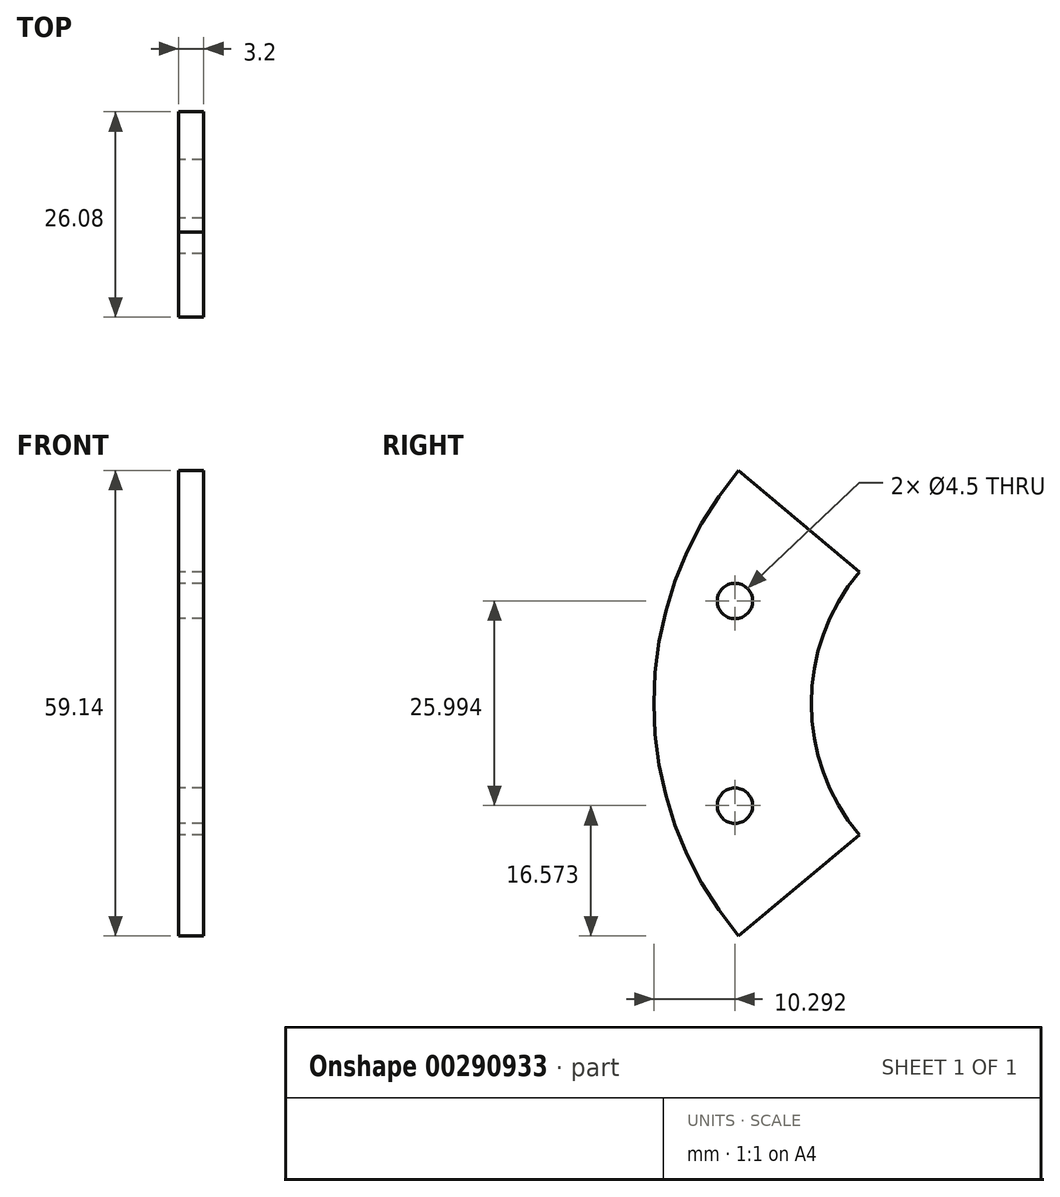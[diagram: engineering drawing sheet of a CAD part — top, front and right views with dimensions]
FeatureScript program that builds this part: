
annotation { "Feature Type Name" : "Feature", "Feature Type Description" : "" }
export const myFeature = defineFeature(function(context is Context, id is Id, definition is map)
    precondition{}
    {
        {
            var Q0;
            Q0=qCreatedBy(makeId("Right.planeOp"),FACE);
            var sketch = newSketch(context, id + "F0", { "sketchPlane" : qUnion([Q0])});
            skArc(sketch, "E0", {"start": v(-19.92, 16.71) * mm, "mid": v(-26, 0) * mm, "end": v(-19.92, -16.71) * mm});
            skArc(sketch, "E1", {"start": v(-35.24, 29.57) * mm, "mid": v(-46, 0) * mm, "end": v(-35.24, -29.57) * mm});
            skCircle(sketch, "E2", {"center": v(0, 0) * mm, "radius": 38 * mm, "construction": true});
            skLineSegment(sketch, "E3", {"start": v(-19.92, 16.71) * mm, "end": v(-35.24, 29.57) * mm});
            skLineSegment(sketch, "E4", {"start": v(0, 0) * mm, "end": v(-56.56, 20.59) * mm, "construction": true});
            skCircle(sketch, "E5", {"center": v(-35.7, 13) * mm, "radius": 2.25 * mm});
            skCircle(sketch, "E6.MirrorC", {"center": v(-35.7, -13) * mm, "radius": 2.25 * mm});
            skLineSegment(sketch, "E7.MirrorCS", {"start": v(-19.92, -16.71) * mm, "end": v(-35.24, -29.57) * mm});
            skPoint(sketch, "E8.orphan", {"position": v(-49.2, 41.28) * mm});
            skPoint(sketch, "E9.orphan", {"position": v(-49.2, -41.28) * mm});
            skSolve(sketch);
        }
        {
            var Q0;
            Q0 = qSketchRegion(id + "F0", true);
            extrude(context, id + "F1", {"entities" : qUnion([Q0]), "depth" : 3.2 * mm});
        }
    });
